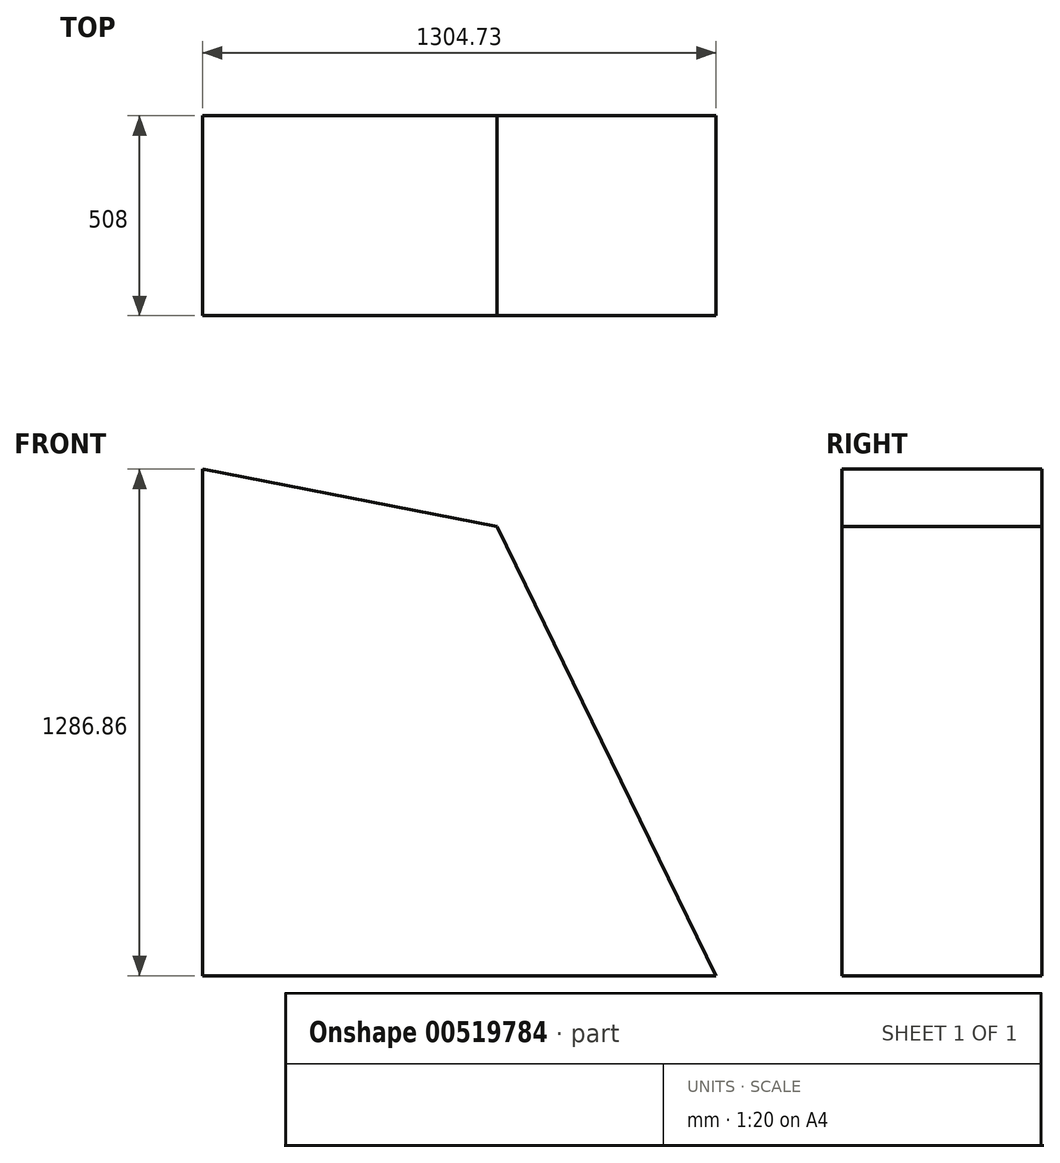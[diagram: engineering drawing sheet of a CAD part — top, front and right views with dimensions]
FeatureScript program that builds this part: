
annotation { "Feature Type Name" : "Feature", "Feature Type Description" : "" }
export const myFeature = defineFeature(function(context is Context, id is Id, definition is map)
    precondition{}
    {
        {
            var Q0;
            Q0=qCreatedBy(makeId("Front.planeOp"),FACE);
            var sketch = newSketch(context, id + "F0", { "sketchPlane" : qUnion([Q0])});
            skLineSegment(sketch, "E0", {"start": v(-1208.25, 0) * mm, "end": v(96.48, 0) * mm});
            skLineSegment(sketch, "E1", {"start": v(96.48, 0) * mm, "end": v(-460.25, 1141.47) * mm});
            skLineSegment(sketch, "E2", {"start": v(-460.25, 1141.47) * mm, "end": v(-1208.25, 1286.86) * mm});
            skLineSegment(sketch, "E3", {"start": v(-1208.25, 1286.86) * mm, "end": v(-1208.25, 0) * mm});
            skSolve(sketch);
        }
        {
            var Q0;
            Q0=makeQuery(id+"F0.imprint","IMPRINT",FACE,{"disambiguationData":[TD([[makeQuery(id+"F0.imprint","IMPRINT",EDGE,{"derivedFrom":sQuery(id+"F0.wireOp",EDGE,"E0")}),1.0]])]});
            extrude(context, id + "F1", {"entities" : qUnion([Q0]), "depth" : 508 * mm, "offsetDistance" : 25.4 * mm});
        }
    });
